# Revit family: Storage-Teknion-CT1E_Single_Tower_Elevated-R2021
name_source: partatom
category: Furniture
units: mm (PartAtom-declared; Revit-internal decimal feet)

## family parameters
Always vertical = Yes
Cut with Voids When Loaded = No
OmniClass Number = 23.40.20.00
OmniClass Title = General Furniture and Specialties
Room Calculation Point = No
Shared = Yes
Work Plane-Based = No

## types (5) — shared parameters
Assembly Code = E2020200
Manufacturer = Teknion
Manufacturer Fax = 416.661.4586
Part Number = CT1E
Product Documentation Link = https://www.teknion.com
Product Line = Bookcases, Stackers & Towers
Product Page URL = https://www.teknion.com
Series = Chronicle
Shelf 5/Top 5E = Yes
Sustainability Data = https://www.teknion.com
URL = www.teknion.com
Unit Weight URL = http://www.teknion.com
Warranty = http://www.teknion.com
Width = 18 "
zero-valued in all types: Default Elevation

## per-type parameters (varying)
| type | Cut-Out - Front 1 | Cut-Out - Front 2 | Cut-Out - Front 3 | Description | Drawer | HF - Hinged Door With Internal Shelves Full Height | Model | OH - Open Upper, Hinged Door Lower | OX - Open Upper, 1 Box 1 File Lower | Shelf 1 | Shelf 2 | Shelf 2 - Front Distance | Shelf 2 - Thickness | Shelf 3 | WW - Wardrobe Full Height | WX - Wardrobe Upper, 1 Box 1 File Lower |
| Hinged Door With Internal Shelves Full Height (HF) | 0.5 " | 0.5 " | 0.5 " | Single Tower, Elevated, Hinged Door With Internal Shelves Full Height Configuration, 18" Width | No | Yes | CT1EHF___18__ | No | No | Yes | Yes | 1.843 " | 1.039 " | Yes | No | No |
| Wardrobe Full Height (WW) | 0.5 " | 0.5 " | 0.5 " | Single Tower, Elevated, Wardrobe Full Height Configuration, 18" Width | No | No | CT1EWW___18__ | No | No | Yes | No | 1.843 " | 1.039 " | No | Yes | No |
| Open Upper, 1 Box 1 File Lower (OX) | 4 " | 0.5 " | 5 " | Single Tower, Elevated, Open Upper, 1 Box 1 File Lower Configuration, 18" Width | Yes | No | CT1EOX___18__ | No | Yes | No | Yes | 0.843 " | 0.724 " | Yes | No | No |
| Open Upper, Hinged Door Lower (OH) | 0.5 " | 0.5 " | 5 " | Single Tower, Elevated, Open Upper, Hinged Door Lower Configuration, 18" Width | No | No | CT1EOH___18__ | Yes | No | Yes | Yes | 0.843 " | 0.724 " | Yes | No | No |
| Wardrobe Upper, 1 Box 1 File Lower (WX) | 4 " | 4 " | 0.5 " | Single Tower, Elevated, Wardrobe Upper, 1 Box 1 File Lower Configuration, 18" Width | Yes | No | CT1EWX___18__ | No | No | No | Yes | 0.843 " | 0.724 " | No | No | Yes |

## geometry (parser evidence)
native form markers: Sweep x3
no freeform markers — native parametric forms only
